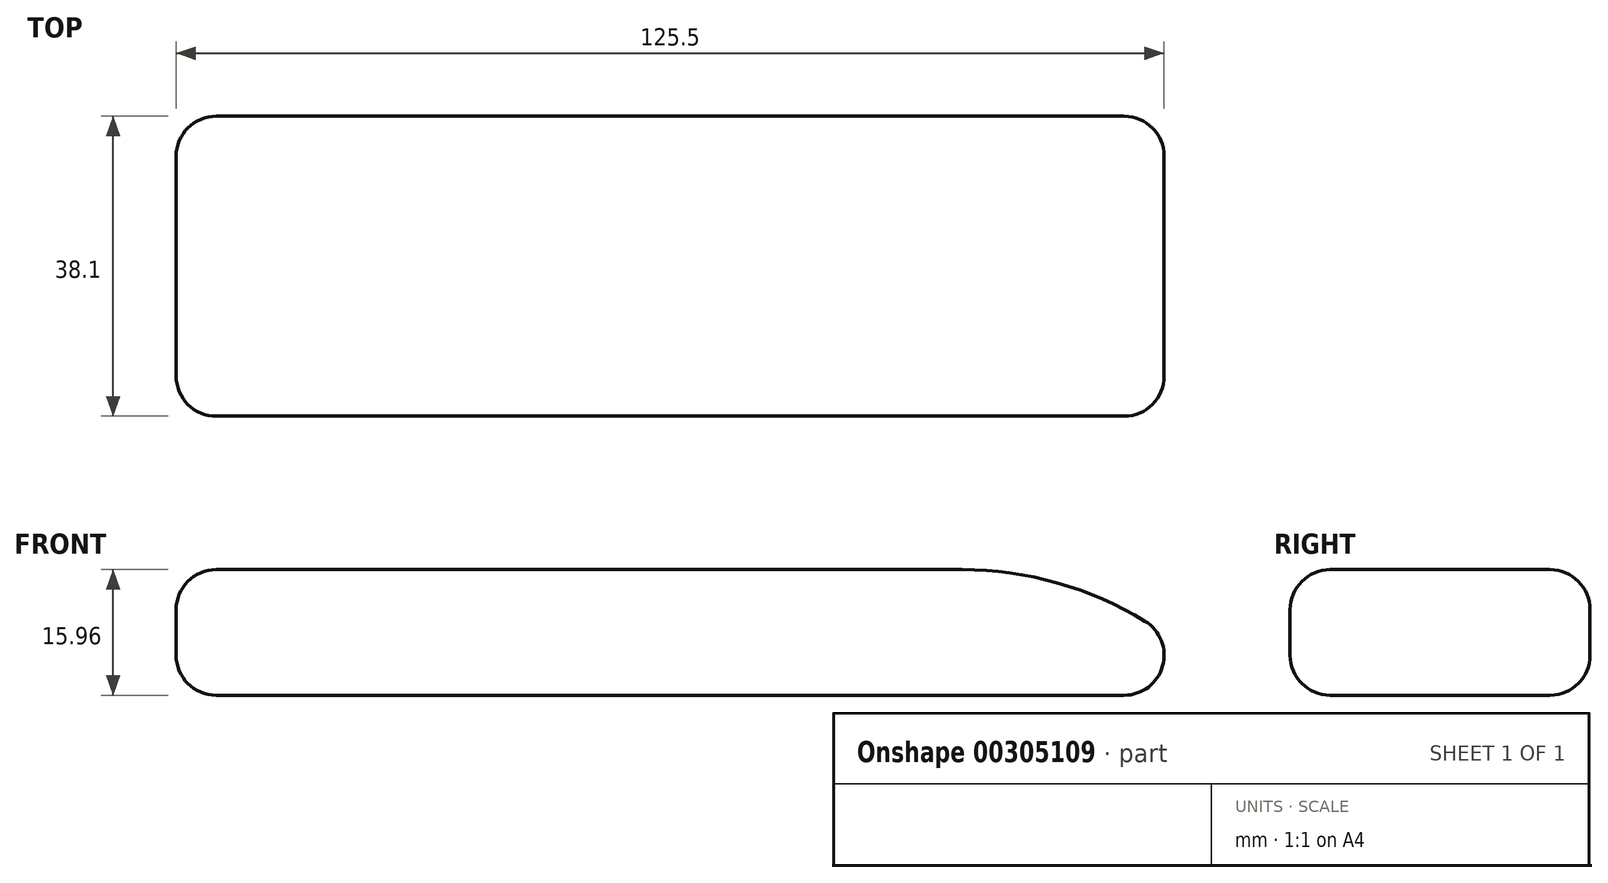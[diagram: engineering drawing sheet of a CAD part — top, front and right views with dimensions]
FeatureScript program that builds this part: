
annotation { "Feature Type Name" : "Feature", "Feature Type Description" : "" }
export const myFeature = defineFeature(function(context is Context, id is Id, definition is map)
    precondition{}
    {
        {
            var Q0;
            Q0=qCreatedBy(makeId("Front.planeOp"),FACE);
            var sketch = newSketch(context, id + "F0", { "sketchPlane" : qUnion([Q0])});
            skLineSegment(sketch, "E0", {"start": v(-89.88, 7.77) * mm, "end": v(-89.88, -8.2) * mm});
            skLineSegment(sketch, "E1", {"start": v(-89.88, -8.2) * mm, "end": v(44.1, -8.2) * mm});
            skLineSegment(sketch, "E2", {"start": v(-89.88, 7.77) * mm, "end": v(9.96, 7.77) * mm});
            skArc(sketch, "E3", {"start": v(44.1, -8.2) * mm, "mid": v(28.8, 3.58) * mm, "end": v(9.96, 7.77) * mm});
            skSolve(sketch);
        }
        {
            var Q0;
            Q0 = qSketchRegion(id + "F0", true);
            extrude(context, id + "F1", {"entities" : qUnion([Q0]), "depth" : 38.1 * mm});
        }
        {
            var Q0;
            Q0=makeQuery(id+"F1.opExtrude","SWEPT_EDGE",EDGE,{"disambiguationData":[OSD([sQuery(id+"F0.wireOp",EDGE,"E0"),sQuery(id+"F0.wireOp",EDGE,"E1")])]});
            var Q1;
            Q1=makeQuery(id+"F1.opExtrude","CAP_EDGE",EDGE,{"disambiguationData":[OSD([sQuery(id+"F0.wireOp",EDGE,"E0")])],"isStart":true});
            var Q2;
            Q2=makeQuery(id+"F1.opExtrude","SWEPT_EDGE",EDGE,{"disambiguationData":[OSD([sQuery(id+"F0.wireOp",EDGE,"E0"),sQuery(id+"F0.wireOp",EDGE,"E2")])]});
            var Q3;
            Q3=makeQuery(id+"F1.opExtrude","CAP_EDGE",EDGE,{"disambiguationData":[OSD([sQuery(id+"F0.wireOp",EDGE,"E0")])],"isStart":false});
            fillet(context, id + "F2", {"entities" : qUnion([Q0, Q1, Q2, Q3]), "radius" : 5.08 * mm, "tangentPropagation" : true, "allowEdgeOverflow" : false});
        }
        {
            var Q0;
            Q0=makeQuery(id+"F1.opExtrude","CAP_EDGE",EDGE,{"disambiguationData":[OSD([sQuery(id+"F0.wireOp",EDGE,"E2")])],"isStart":false});
            var Q1;
            Q1=makeQuery(id+"F1.opExtrude","CAP_EDGE",EDGE,{"disambiguationData":[OSD([sQuery(id+"F0.wireOp",EDGE,"E1")])],"isStart":false});
            var Q2;
            Q2=makeQuery(id+"F1.opExtrude","SWEPT_EDGE",EDGE,{"disambiguationData":[OSD([sQuery(id+"F0.wireOp",EDGE,"E1"),sQuery(id+"F0.wireOp",EDGE,"E3")])]});
            var Q3;
            Q3=makeQuery(id+"F1.opExtrude","SWEPT_FACE",FACE,{"disambiguationData":[OSD([sQuery(id+"F0.wireOp",EDGE,"E3")])]});
            var Q4;
            Q4=makeQuery(id+"F1.opExtrude","CAP_EDGE",EDGE,{"disambiguationData":[OSD([sQuery(id+"F0.wireOp",EDGE,"E1")])],"isStart":true});
            var Q5;
            {var subQ0=sQuery(id+"F0.wireOp",EDGE,"E0");Q5=makeQuery(id+"F2.opFillet","BLEND_EDGE",EDGE,{"blendedFrom":[makeQuery(id+"F1.opExtrude","CAP_EDGE",EDGE,{"disambiguationData":[OSD([subQ0])],"isStart":true}),makeQuery(id+"F1.opExtrude","CAP_FACE",FACE,{"disambiguationData":[OSD([subQ0,sQuery(id+"F0.wireOp",EDGE,"E1"),sQuery(id+"F0.wireOp",EDGE,"E2"),sQuery(id+"F0.wireOp",EDGE,"E3")])],"isStart":true})],"blendedInto":[makeQuery(id+"F1.opExtrude","CAP_FACE",FACE,{"disambiguationData":[OSD([subQ0,sQuery(id+"F0.wireOp",EDGE,"E1"),sQuery(id+"F0.wireOp",EDGE,"E2"),sQuery(id+"F0.wireOp",EDGE,"E3")])],"isStart":true})]});}
            var Q6;
            {var subQ0=sQuery(id+"F0.wireOp",EDGE,"E0");Q6=makeQuery(id+"F2.opFillet","BLEND_EDGE",EDGE,{"blendedFrom":[makeQuery(id+"F1.opExtrude","SWEPT_EDGE",EDGE,{"disambiguationData":[OSD([subQ0,sQuery(id+"F0.wireOp",EDGE,"E1")])]}),makeQuery(id+"F1.opExtrude","CAP_EDGE",EDGE,{"disambiguationData":[OSD([subQ0])],"isStart":true})],"blendedInto":[]});}
            var Q7;
            {var subQ0=sQuery(id+"F0.wireOp",EDGE,"E0");Q7=makeQuery(id+"F2.opFillet","BLEND_EDGE",EDGE,{"blendedFrom":[makeQuery(id+"F1.opExtrude","SWEPT_EDGE",EDGE,{"disambiguationData":[OSD([subQ0,sQuery(id+"F0.wireOp",EDGE,"E2")])]}),makeQuery(id+"F1.opExtrude","CAP_EDGE",EDGE,{"disambiguationData":[OSD([subQ0])],"isStart":true})],"blendedInto":[]});}
            var Q8;
            {var subQ0=sQuery(id+"F0.wireOp",EDGE,"E0");Q8=makeQuery(id+"F2.opFillet","BLEND_EDGE",EDGE,{"blendedFrom":[makeQuery(id+"F1.opExtrude","SWEPT_EDGE",EDGE,{"disambiguationData":[OSD([subQ0,sQuery(id+"F0.wireOp",EDGE,"E2")])]}),makeQuery(id+"F1.opExtrude","CAP_EDGE",EDGE,{"disambiguationData":[OSD([subQ0])],"isStart":false})],"blendedInto":[]});}
            var Q9;
            {var subQ0=sQuery(id+"F0.wireOp",EDGE,"E0");Q9=makeQuery(id+"F2.opFillet","BLEND_EDGE",EDGE,{"blendedFrom":[makeQuery(id+"F1.opExtrude","SWEPT_EDGE",EDGE,{"disambiguationData":[OSD([subQ0,sQuery(id+"F0.wireOp",EDGE,"E1")])]}),makeQuery(id+"F1.opExtrude","CAP_EDGE",EDGE,{"disambiguationData":[OSD([subQ0])],"isStart":false})],"blendedInto":[]});}
            fillet(context, id + "F3", {"entities" : qUnion([Q0, Q1, Q2, Q3, Q4, Q5, Q6, Q7, Q8, Q9]), "radius" : 5.08 * mm, "tangentPropagation" : true, "allowEdgeOverflow" : false});
        }
    });
